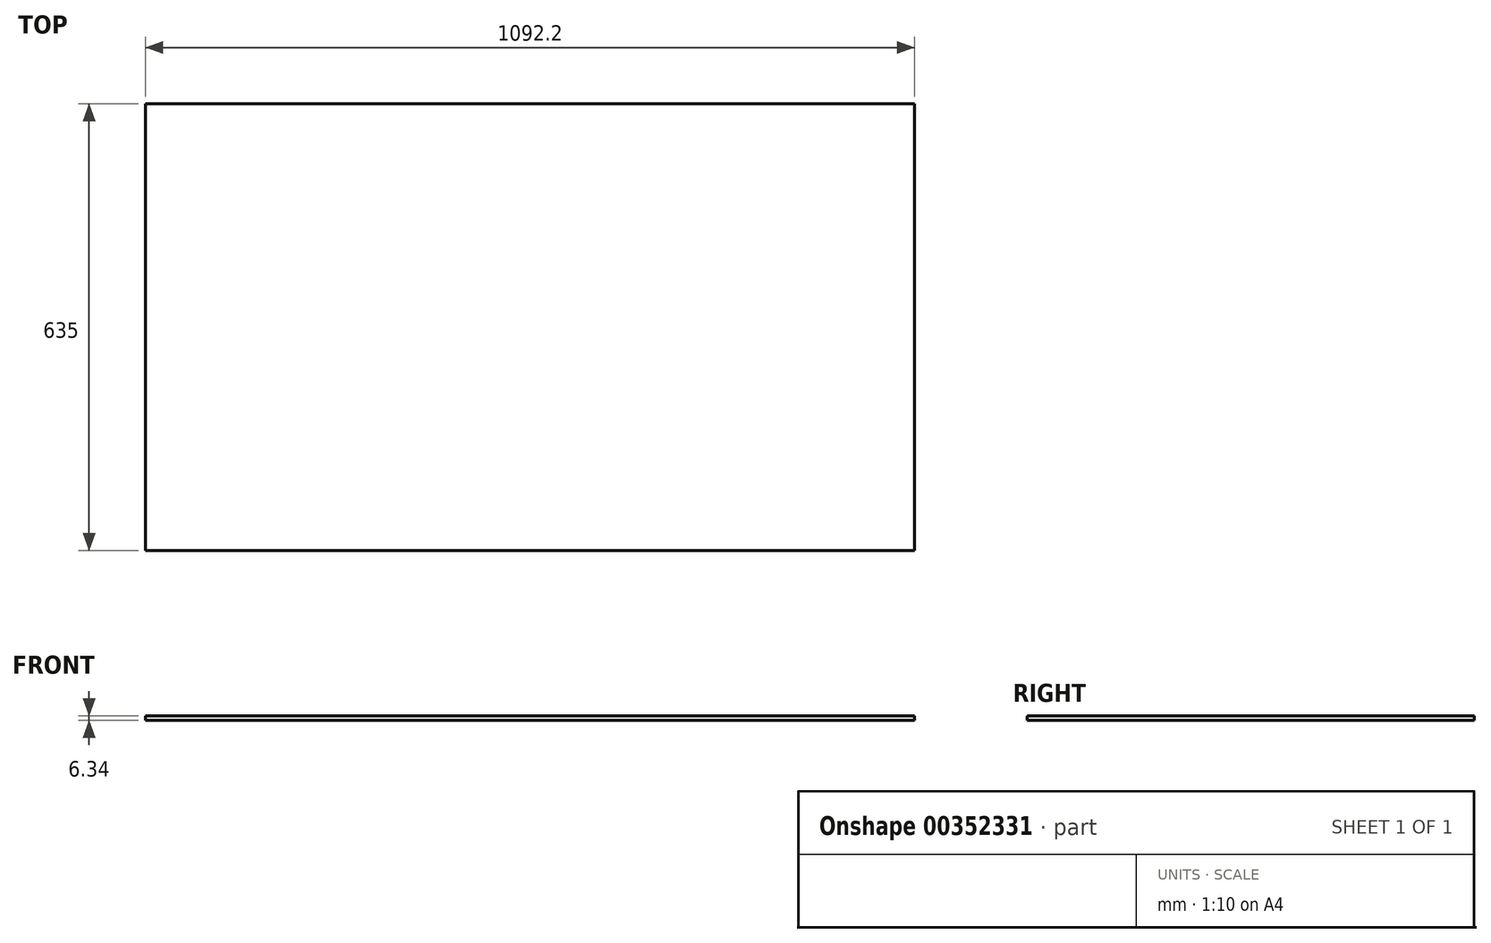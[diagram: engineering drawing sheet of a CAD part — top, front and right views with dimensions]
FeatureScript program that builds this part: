
annotation { "Feature Type Name" : "Feature", "Feature Type Description" : "" }
export const myFeature = defineFeature(function(context is Context, id is Id, definition is map)
    precondition{}
    {
        {
            var Q0;
            Q0=qCreatedBy(makeId("Top.planeOp"),FACE);
            var sketch = newSketch(context, id + "F0", { "sketchPlane" : qUnion([Q0])});
            skLineSegment(sketch, "E0.bottom", {"start": v(546.1, 317.5) * mm, "end": v(-546.1, 317.5) * mm});
            skLineSegment(sketch, "E0.top", {"start": v(546.1, -317.5) * mm, "end": v(-546.1, -317.5) * mm});
            skLineSegment(sketch, "E0.left", {"start": v(546.1, 317.5) * mm, "end": v(546.1, -317.5) * mm});
            skLineSegment(sketch, "E0.right", {"start": v(-546.1, 317.5) * mm, "end": v(-546.1, -317.5) * mm});
            skPoint(sketch, "E0.middle", {"position": v(0, 0) * mm});
            skSolve(sketch);
        }
        {
            var Q0;
            Q0=makeQuery(id+"F0.imprint","IMPRINT",FACE,{"disambiguationData":[TD([[makeQuery(id+"F0.imprint","IMPRINT",EDGE,{"derivedFrom":sQuery(id+"F0.wireOp",EDGE,"E0.bottom")}),1.0]])]});
            extrude(context, id + "F1", {"entities" : qUnion([Q0]), "endBound" : BoundingType.SYMMETRIC, "depth" : 6.35 * mm});
        }
    });
